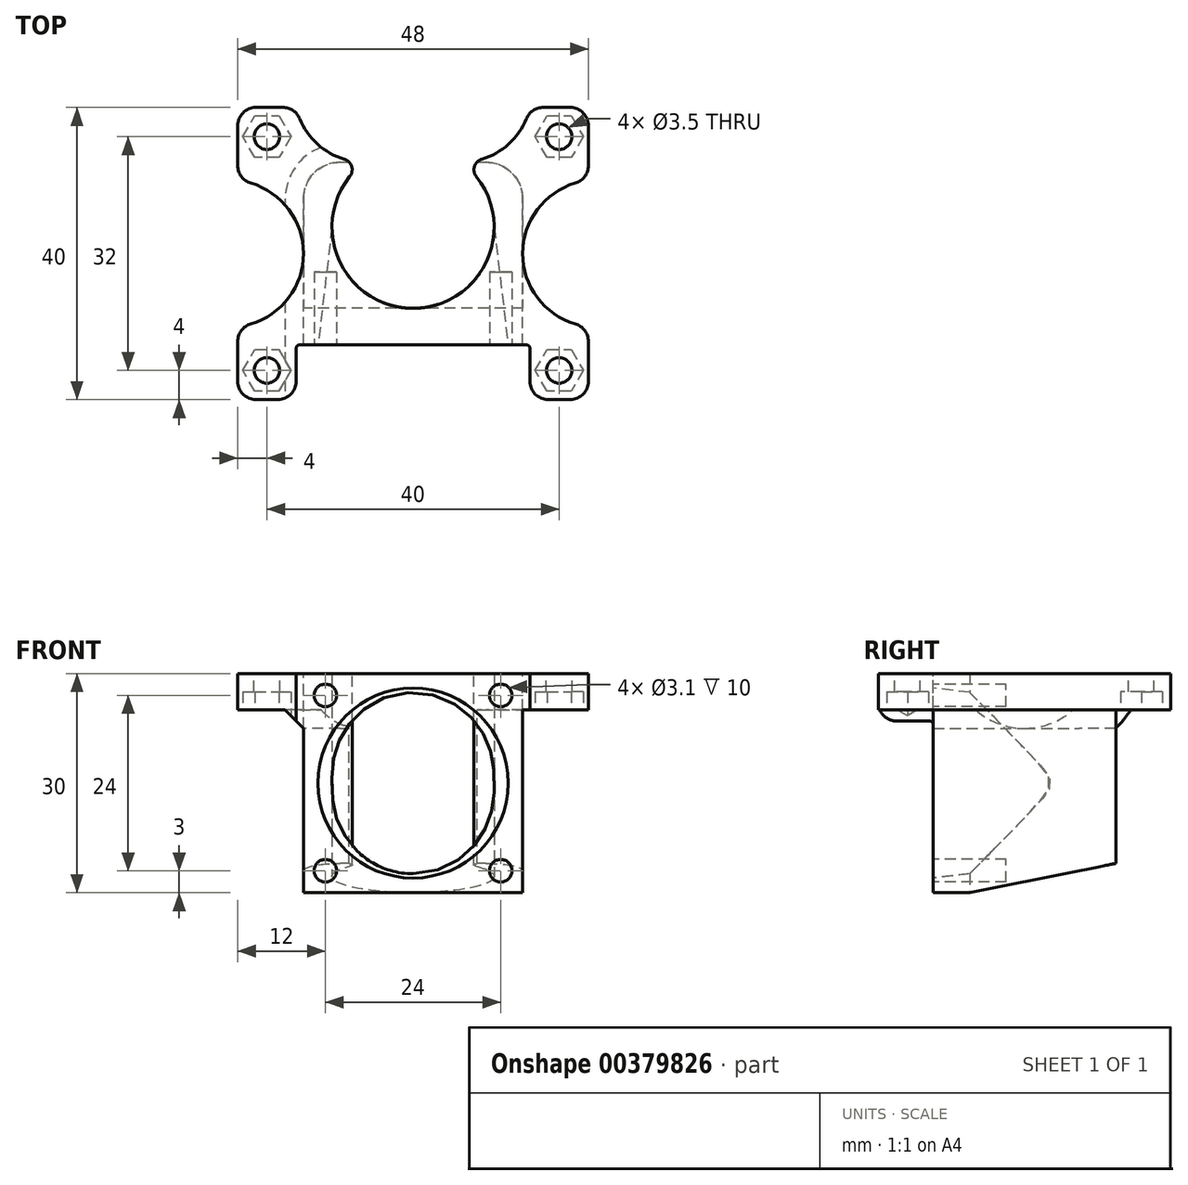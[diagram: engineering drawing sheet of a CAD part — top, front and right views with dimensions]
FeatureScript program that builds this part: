
annotation { "Feature Type Name" : "Feature", "Feature Type Description" : "" }
export const myFeature = defineFeature(function(context is Context, id is Id, definition is map)
    precondition{}
    {
        {
            var Q0;
            Q0=qCreatedBy(makeId("Top.planeOp"),FACE);
            var sketch = newSketch(context, id + "F0", { "sketchPlane" : qUnion([Q0])});
            skLineSegment(sketch, "E0.bottom", {"start": v(0, 0) * mm, "end": v(30, 0) * mm});
            skLineSegment(sketch, "E0.top", {"start": v(0, 25) * mm, "end": v(8.37, 25) * mm});
            skLineSegment(sketch, "E0.left", {"start": v(0, 0) * mm, "end": v(0, 25) * mm});
            skLineSegment(sketch, "E0.right", {"start": v(30, 0) * mm, "end": v(30, 25) * mm});
            skArc(sketch, "E1", {"start": v(8.37, 25) * mm, "mid": v(15, 5) * mm, "end": v(21.63, 25) * mm});
            skPoint(sketch, "E1.centerSnap0", {"position": v(15, 25) * mm});
            skLineSegment(sketch, "E2.trimOffspring", {"start": v(21.63, 25) * mm, "end": v(30, 25) * mm});
            skSolve(sketch);
        }
        {
            var Q0;
            Q0=qSketchRegion(id+"F0",true);
            extrude(context, id + "F1", {"entities" : qUnion([Q0]), "depth" : 30 * mm});
        }
        {
            var Q0;
            Q0=makeQuery(id+"F1.opExtrude","SWEPT_FACE",FACE,{"disambiguationData":[OSD([sQuery(id+"F0.wireOp",EDGE,"E0.left")])]});
            var sketch = newSketch(context, id + "F2", { "sketchPlane" : qUnion([Q0])});
            skLineSegment(sketch, "E3", {"start": v(-25, 4) * mm, "end": v(-5, 0) * mm});
            skLineSegment(sketch, "E4", {"start": v(-5, 0) * mm, "end": v(-25, 0) * mm});
            skLineSegment(sketch, "E5", {"start": v(-25, 0) * mm, "end": v(-25, 4) * mm});
            skSolve(sketch);
        }
        {
            var Q0;
            Q0=makeQuery(id+"F2.imprint","IMPRINT",FACE,{"disambiguationData":[TD([[makeQuery(id+"F2.imprint","IMPRINT",EDGE,{"derivedFrom":sQuery(id+"F2.wireOp",EDGE,"E3")}),-1.0]])]});
            extrude(context, id + "F3", {"entities" : qUnion([Q0]), "operationType" : NewBodyOperationType.REMOVE, "endBound" : BoundingType.THROUGH_ALL, "oppositeDirection" : true, "depth" : 25 * mm});
        }
        {
            var Q0;
            Q0=makeQuery(id+"F1.opExtrude","CAP_FACE",FACE,{"disambiguationData":[OSD([sQuery(id+"F0.wireOp",EDGE,"E0.bottom"),sQuery(id+"F0.wireOp",EDGE,"E0.top"),sQuery(id+"F0.wireOp",EDGE,"E0.left"),sQuery(id+"F0.wireOp",EDGE,"E0.right"),sQuery(id+"F0.wireOp",EDGE,"E1"),sQuery(id+"F0.wireOp",EDGE,"E2.trimOffspring")])],"isStart":false});
            cPlane(context, id + "F4", {"entities" : qUnion([Q0]), "cplaneType" : CPlaneType.OFFSET, "offset" : 15 * mm, "oppositeDirection" : true, "width" : 150 * mm, "height" : 150 * mm});
        }
        {
            var Q0;
            Q0=qCreatedBy(id+"F4.planeOp",FACE);
            var sketch = newSketch(context, id + "F5", { "sketchPlane" : qUnion([Q0])});
            skArc(sketch, "E6.0.0", {"start": v(15, 5) * mm, "mid": v(7.15, 8.25) * mm, "end": v(3.9, 16.1) * mm});
            skLineSegment(sketch, "E6.0.1", {"start": v(8.37, 25) * mm, "end": v(0, 25) * mm, "construction": true});
            skLineSegment(sketch, "E6.0.2", {"start": v(0, 25) * mm, "end": v(0, 0) * mm, "construction": true});
            skLineSegment(sketch, "E6.0.3", {"start": v(0, 0) * mm, "end": v(30, 0) * mm, "construction": true});
            skLineSegment(sketch, "E6.0.4", {"start": v(30, 0) * mm, "end": v(30, 25) * mm, "construction": true});
            skLineSegment(sketch, "E6.0.5", {"start": v(30, 25) * mm, "end": v(21.63, 25) * mm, "construction": true});
            skLineSegment(sketch, "E7", {"start": v(3.9, 16.1) * mm, "end": v(2, 0) * mm});
            skLineSegment(sketch, "E8", {"start": v(2, 0) * mm, "end": v(15, 0) * mm});
            skLineSegment(sketch, "E9", {"start": v(15, 0) * mm, "end": v(15, 5) * mm});
            skLineSegment(sketch, "E10", {"start": v(15, 16.1) * mm, "end": v(15, 5) * mm, "construction": true});
            skSolve(sketch);
        }
        {
            var Q0;
            Q0=qSketchRegion(id+"F5",true);
            var Q1;
            Q1=sQuery(id+"F5.wireOp",EDGE,"E10");
            revolve(context, id + "F6", {"operationType" : NewBodyOperationType.REMOVE, "entities" : qUnion([Q0]), "axis" : qUnion([Q1]), "revolveType" : RevolveType.FULL, "oppositeDirection" : true});
        }
        {
            var Q0;
            Q0=makeQuery(id+"F1.opExtrude","SWEPT_FACE",FACE,{"disambiguationData":[OSD([sQuery(id+"F0.wireOp",EDGE,"E0.bottom")])]});
            var sketch = newSketch(context, id + "F7", { "sketchPlane" : qUnion([Q0])});
            skCircle(sketch, "E11", {"center": v(3, 27) * mm, "radius": 1.55 * mm});
            skCircle(sketch, "E12", {"center": v(27, 27) * mm, "radius": 1.55 * mm});
            skCircle(sketch, "E13", {"center": v(27, 3) * mm, "radius": 1.55 * mm});
            skCircle(sketch, "E14", {"center": v(3, 3) * mm, "radius": 1.55 * mm});
            skSolve(sketch);
        }
        {
            var Q0;
            Q0=qSketchRegion(id+"F7",true);
            extrude(context, id + "F8", {"entities" : qUnion([Q0]), "operationType" : NewBodyOperationType.REMOVE, "oppositeDirection" : true, "depth" : 10 * mm});
        }
        {
            var Q0;
            Q0=makeQuery(id+"F1.opExtrude","CAP_FACE",FACE,{"disambiguationData":[OSD([sQuery(id+"F0.wireOp",EDGE,"E0.bottom"),sQuery(id+"F0.wireOp",EDGE,"E0.top"),sQuery(id+"F0.wireOp",EDGE,"E0.left"),sQuery(id+"F0.wireOp",EDGE,"E0.right"),sQuery(id+"F0.wireOp",EDGE,"E1"),sQuery(id+"F0.wireOp",EDGE,"E2.trimOffspring")])],"isStart":false});
            var sketch = newSketch(context, id + "F9", { "sketchPlane" : qUnion([Q0])});
            skCircle(sketch, "E15", {"center": v(35, -3.5) * mm, "radius": 1.75 * mm});
            skCircle(sketch, "E16", {"center": v(35, 28.5) * mm, "radius": 1.75 * mm});
            skLineSegment(sketch, "E17", {"start": v(31, 32.5) * mm, "end": v(39, 32.5) * mm});
            skLineSegment(sketch, "E18", {"start": v(39, 32.5) * mm, "end": v(39, 22.5) * mm});
            skPoint(sketch, "E19", {"position": v(30, 12.5) * mm});
            skLineSegment(sketch, "E20", {"start": v(30, 12.5) * mm, "end": v(39, 12.5) * mm, "construction": true});
            skLineSegment(sketch, "E21.MirrorCS", {"start": v(39, -7.5) * mm, "end": v(39, 2.5) * mm});
            skLineSegment(sketch, "E22.MirrorCS", {"start": v(31, -7.5) * mm, "end": v(39, -7.5) * mm});
            skLineSegment(sketch, "E23.MirrorCS", {"start": v(31, 0) * mm, "end": v(31, -7.5) * mm});
            skLineSegment(sketch, "E24.MirrorCS", {"start": v(30, 0) * mm, "end": v(31, 0) * mm});
            skLineSegment(sketch, "E25", {"start": v(15, 0) * mm, "end": v(15, 5) * mm, "construction": true});
            skLineSegment(sketch, "E26", {"start": v(30, 25) * mm, "end": v(21.63, 25) * mm});
            skArc(sketch, "E27", {"start": v(21.63, 25) * mm, "mid": v(27.63, 27.1) * mm, "end": v(31, 32.5) * mm});
            skArc(sketch, "E28", {"start": v(39, 22.5) * mm, "mid": v(30, 12.5) * mm, "end": v(39, 2.5) * mm});
            skLineSegment(sketch, "E29", {"start": v(30, 25) * mm, "end": v(30, 0) * mm});
            skLineSegment(sketch, "E30.MirrorCS", {"start": v(0, 0) * mm, "end": v(-1, 0) * mm});
            skLineSegment(sketch, "E31.MirrorCS", {"start": v(0, 25) * mm, "end": v(0, 0) * mm});
            skCircle(sketch, "E32.MirrorC", {"center": v(-5, -3.5) * mm, "radius": 1.75 * mm});
            skLineSegment(sketch, "E33.MirrorCS", {"start": v(-1, 32.5) * mm, "end": v(-9, 32.5) * mm});
            skLineSegment(sketch, "E34.MirrorCS", {"start": v(-9, -7.5) * mm, "end": v(-9, 2.5) * mm});
            skLineSegment(sketch, "E35.MirrorCS", {"start": v(-1, -7.5) * mm, "end": v(-9, -7.5) * mm});
            skLineSegment(sketch, "E36.MirrorCS", {"start": v(-9, 32.5) * mm, "end": v(-9, 22.5) * mm});
            skCircle(sketch, "E37.MirrorC", {"center": v(-5, 28.5) * mm, "radius": 1.75 * mm});
            skLineSegment(sketch, "E38.MirrorCS", {"start": v(0, 25) * mm, "end": v(8.37, 25) * mm});
            skPoint(sketch, "E39.MirrorP", {"position": v(0, 12.5) * mm});
            skLineSegment(sketch, "E40.MirrorCS", {"start": v(-1, 0) * mm, "end": v(-1, -7.5) * mm});
            skArc(sketch, "E41.MirrorCS", {"start": v(-9, 22.5) * mm, "mid": v(0, 12.5) * mm, "end": v(-9, 2.5) * mm});
            skArc(sketch, "E42.MirrorCS", {"start": v(8.37, 25) * mm, "mid": v(2.37, 27.1) * mm, "end": v(-1, 32.5) * mm});
            skLineSegment(sketch, "E43.MirrorCS", {"start": v(0, 12.5) * mm, "end": v(-9, 12.5) * mm, "construction": true});
            skSolve(sketch);
        }
        {
            var Q0;
            Q0=qSketchRegion(id+"F9",true);
            extrude(context, id + "F10", {"entities" : qUnion([Q0]), "operationType" : NewBodyOperationType.ADD, "oppositeDirection" : true, "depth" : 5 * mm});
        }
        {
            var Q0;
            {var subQ0=sQuery(id+"F0.wireOp",EDGE,"E0.top");var subQ1=sQuery(id+"F9.wireOp",EDGE,"fd6141a5-e393-4f37-ba07-f76781136fbe3.MirrorCS");Q0=makeQuery(id+"F10.boolean.opBoolean","SPLIT",EDGE,{"disambiguationData":[topologyDisambiguationEdgeConnected([makeQuery(id+"F10.opExtrude","SWEPT_FACE",FACE,{"disambiguationData":[OSD([subQ1]),TDD([makeQuery(id+"F9.imprint","IMPRINT",EDGE,{"disambiguationData":[TD([[makeQuery(id+"F9.imprint","INTERSECT",VERTEX,{"derivedFrom":[sQuery(id+"F9.wireOp",EDGE,"fd6141a5-e393-4f37-ba07-f76781136fbe2.MirrorCS"),subQ1]}),-1.0]])],"derivedFrom":subQ1}),makeQuery(id+"F9.imprint","IMPRINT",EDGE,{"disambiguationData":[TD([[makeQuery(id+"F9.imprint","INTERSECT",VERTEX,{"derivedFrom":[sQuery(id+"F9.wireOp",EDGE,"fd6141a5-e393-4f37-ba07-f76781136fbe1.MirrorCS"),subQ1]}),-1.0]])],"derivedFrom":subQ1})])]})])],"derivedFrom":makeQuery(id+"F1.opExtrude","SWEPT_EDGE",EDGE,{"disambiguationData":[OSD([subQ0,sQuery(id+"F0.wireOp",EDGE,"E0.left")])]})});}
            var Q1;
            {var subQ0=sQuery(id+"F0.wireOp",EDGE,"E2.trimOffspring");var subQ1=sQuery(id+"F9.wireOp",EDGE,"lfwtUtIS-q4o2-o8Hh-EETJ-Xmfctvlnuw40");Q1=makeQuery(id+"F10.boolean.opBoolean","SPLIT",EDGE,{"disambiguationData":[topologyDisambiguationEdgeConnected([makeQuery(id+"F10.opExtrude","SWEPT_FACE",FACE,{"disambiguationData":[OSD([subQ1]),TDD([makeQuery(id+"F9.imprint","IMPRINT",EDGE,{"disambiguationData":[TD([[makeQuery(id+"F9.imprint","INTERSECT",VERTEX,{"derivedFrom":[sQuery(id+"F9.wireOp",EDGE,"dHIleryw-Gs0o-nNQL-AnOp-lo5zabTGxiNF"),subQ1]}),-1.0]])],"derivedFrom":subQ1}),makeQuery(id+"F9.imprint","IMPRINT",EDGE,{"disambiguationData":[TD([[makeQuery(id+"F9.imprint","INTERSECT",VERTEX,{"derivedFrom":[subQ1,sQuery(id+"F9.wireOp",EDGE,"BK98jPus-1Hkl-NgJk-qqdw-X6xCajcux68K")]}),-1.0]])],"derivedFrom":subQ1})])]})])],"derivedFrom":makeQuery(id+"F1.opExtrude","SWEPT_EDGE",EDGE,{"disambiguationData":[OSD([sQuery(id+"F0.wireOp",EDGE,"E0.right"),subQ0])]})});}
            fillet(context, id + "F11", {"entities" : qUnion([Q0, Q1]), "radius" : 5 * mm, "tangentPropagation" : true, "allowEdgeOverflow" : false});
        }
        {
            var Q0;
            {var subQ0=sQuery(id+"F9.wireOp",EDGE,"E41.MirrorCS");var subQ1=sQuery(id+"F9.wireOp",EDGE,"E31.MirrorCS");var subQ2=sQuery(id+"F9.wireOp",EDGE,"E29");var subQ3=sQuery(id+"F9.wireOp",EDGE,"E28");Q0=makeQuery(id+"F10.boolean.opBoolean","MERGE",FACE,{"derivedFrom":[makeQuery(id+"F1.opExtrude","CAP_FACE",FACE,{"disambiguationData":[OSD([sQuery(id+"F0.wireOp",EDGE,"E0.bottom"),sQuery(id+"F0.wireOp",EDGE,"E0.top"),sQuery(id+"F0.wireOp",EDGE,"E0.left"),sQuery(id+"F0.wireOp",EDGE,"E0.right"),sQuery(id+"F0.wireOp",EDGE,"E1"),sQuery(id+"F0.wireOp",EDGE,"E2.trimOffspring")])],"isStart":false}),makeQuery(id+"F10.opExtrude","CAP_FACE",FACE,{"disambiguationData":[OSD([sQuery(id+"F9.wireOp",EDGE,"E15"),sQuery(id+"F9.wireOp",EDGE,"E21.MirrorCS"),sQuery(id+"F9.wireOp",EDGE,"E22.MirrorCS"),sQuery(id+"F9.wireOp",EDGE,"E23.MirrorCS"),sQuery(id+"F9.wireOp",EDGE,"E24.MirrorCS"),subQ3,subQ2])],"isStart":true}),makeQuery(id+"F10.opExtrude","CAP_FACE",FACE,{"disambiguationData":[OSD([sQuery(id+"F9.wireOp",EDGE,"E16"),sQuery(id+"F9.wireOp",EDGE,"E17"),sQuery(id+"F9.wireOp",EDGE,"E18"),sQuery(id+"F9.wireOp",EDGE,"E26"),sQuery(id+"F9.wireOp",EDGE,"E27"),subQ3,subQ2])],"isStart":true}),makeQuery(id+"F10.opExtrude","CAP_FACE",FACE,{"disambiguationData":[OSD([sQuery(id+"F9.wireOp",EDGE,"E30.MirrorCS"),subQ1,sQuery(id+"F9.wireOp",EDGE,"E32.MirrorC"),sQuery(id+"F9.wireOp",EDGE,"E34.MirrorCS"),sQuery(id+"F9.wireOp",EDGE,"E35.MirrorCS"),sQuery(id+"F9.wireOp",EDGE,"E40.MirrorCS"),subQ0])],"isStart":true}),makeQuery(id+"F10.opExtrude","CAP_FACE",FACE,{"disambiguationData":[OSD([subQ1,sQuery(id+"F9.wireOp",EDGE,"E33.MirrorCS"),sQuery(id+"F9.wireOp",EDGE,"E36.MirrorCS"),sQuery(id+"F9.wireOp",EDGE,"E37.MirrorC"),sQuery(id+"F9.wireOp",EDGE,"E38.MirrorCS"),subQ0,sQuery(id+"F9.wireOp",EDGE,"E42.MirrorCS")])],"isStart":true})]});}
            var sketch = newSketch(context, id + "F12", { "sketchPlane" : qUnion([Q0])});
            skArc(sketch, "E44", {"start": v(6.33, 23.04) * mm, "mid": v(6.6, 24.42) * mm, "end": v(5.6, 25.4) * mm});
            skArc(sketch, "E45.0", {"start": v(8.37, 25) * mm, "mid": v(6.97, 25.1) * mm, "end": v(5.6, 25.4) * mm});
            skArc(sketch, "E46.0", {"start": v(8.37, 25) * mm, "mid": v(7.29, 24.08) * mm, "end": v(6.33, 23.04) * mm});
            skLineSegment(sketch, "E47", {"start": v(15, 16.1) * mm, "end": v(15, 25) * mm, "construction": true});
            skArc(sketch, "E48.MirrorCS", {"start": v(23.67, 23.04) * mm, "mid": v(23.4, 24.42) * mm, "end": v(24.4, 25.4) * mm});
            skArc(sketch, "E49.MirrorCS", {"start": v(21.63, 25) * mm, "mid": v(23.03, 25.1) * mm, "end": v(24.4, 25.4) * mm});
            skPoint(sketch, "E50.orphan", {"position": v(31, 32.5) * mm});
            skArc(sketch, "E51.trimOffspring", {"start": v(23.67, 23.04) * mm, "mid": v(22.71, 24.08) * mm, "end": v(21.63, 25) * mm});
            skPoint(sketch, "E52.orphan", {"position": v(-1, 32.5) * mm});
            skSolve(sketch);
        }
        {
            var Q0;
            Q0=qSketchRegion(id+"F12",true);
            extrude(context, id + "F13", {"entities" : qUnion([Q0]), "operationType" : NewBodyOperationType.REMOVE, "endBound" : BoundingType.THROUGH_ALL, "oppositeDirection" : true, "depth" : 25 * mm});
        }
        {
            var Q0;
            Q0=makeQuery(id+"F10.opExtrude","SWEPT_EDGE",EDGE,{"disambiguationData":[OSD([sQuery(id+"F9.wireOp",EDGE,"E33.MirrorCS"),sQuery(id+"F9.wireOp",EDGE,"E36.MirrorCS")])]});
            var Q1;
            Q1=makeQuery(id+"F10.opExtrude","SWEPT_EDGE",EDGE,{"disambiguationData":[OSD([sQuery(id+"F9.wireOp",EDGE,"E36.MirrorCS"),sQuery(id+"F9.wireOp",EDGE,"E41.MirrorCS")])]});
            var Q2;
            Q2=makeQuery(id+"F10.opExtrude","SWEPT_EDGE",EDGE,{"disambiguationData":[OSD([sQuery(id+"F9.wireOp",EDGE,"E34.MirrorCS"),sQuery(id+"F9.wireOp",EDGE,"E41.MirrorCS")])]});
            var Q3;
            Q3=makeQuery(id+"F10.opExtrude","SWEPT_EDGE",EDGE,{"disambiguationData":[OSD([sQuery(id+"F9.wireOp",EDGE,"E34.MirrorCS"),sQuery(id+"F9.wireOp",EDGE,"E35.MirrorCS")])]});
            var Q4;
            Q4=makeQuery(id+"F10.opExtrude","SWEPT_EDGE",EDGE,{"disambiguationData":[OSD([sQuery(id+"F9.wireOp",EDGE,"E35.MirrorCS"),sQuery(id+"F9.wireOp",EDGE,"E40.MirrorCS")])]});
            var Q5;
            Q5=makeQuery(id+"F10.opExtrude","SWEPT_EDGE",EDGE,{"disambiguationData":[OSD([sQuery(id+"F9.wireOp",EDGE,"E18"),sQuery(id+"F9.wireOp",EDGE,"E28")])]});
            var Q6;
            Q6=makeQuery(id+"F10.opExtrude","SWEPT_EDGE",EDGE,{"disambiguationData":[OSD([sQuery(id+"F9.wireOp",EDGE,"E21.MirrorCS"),sQuery(id+"F9.wireOp",EDGE,"E22.MirrorCS")])]});
            var Q7;
            Q7=makeQuery(id+"F10.opExtrude","SWEPT_EDGE",EDGE,{"disambiguationData":[OSD([sQuery(id+"F9.wireOp",EDGE,"E22.MirrorCS"),sQuery(id+"F9.wireOp",EDGE,"E23.MirrorCS")])]});
            var Q8;
            Q8=makeQuery(id+"F10.opExtrude","SWEPT_EDGE",EDGE,{"disambiguationData":[OSD([sQuery(id+"F9.wireOp",EDGE,"E21.MirrorCS"),sQuery(id+"F9.wireOp",EDGE,"E28")])]});
            var Q9;
            Q9=makeQuery(id+"F10.opExtrude","SWEPT_EDGE",EDGE,{"disambiguationData":[OSD([sQuery(id+"F9.wireOp",EDGE,"E17"),sQuery(id+"F9.wireOp",EDGE,"E18")])]});
            var Q10;
            Q10=makeQuery(id+"F10.opExtrude","SWEPT_EDGE",EDGE,{"disambiguationData":[OSD([sQuery(id+"F9.wireOp",EDGE,"E17"),sQuery(id+"F9.wireOp",EDGE,"E27")])]});
            var Q11;
            Q11=makeQuery(id+"F10.opExtrude","SWEPT_EDGE",EDGE,{"disambiguationData":[OSD([sQuery(id+"F9.wireOp",EDGE,"E33.MirrorCS"),sQuery(id+"F9.wireOp",EDGE,"E42.MirrorCS")])]});
            fillet(context, id + "F14", {"entities" : qUnion([Q0, Q1, Q2, Q3, Q4, Q5, Q6, Q7, Q8, Q9, Q10, Q11]), "radius" : 2.5 * mm, "tangentPropagation" : true, "allowEdgeOverflow" : false});
        }
        {
            var Q0;
            {var subQ0=sQuery(id+"F9.wireOp",EDGE,"E29");Q0=makeQuery(id+"F10.opExtrude","CAP_EDGE",EDGE,{"disambiguationData":[OSD([subQ0]),TDD([makeQuery(id+"F9.imprint","IMPRINT",EDGE,{"disambiguationData":[TD([[makeQuery(id+"F9.imprint","INTERSECT",VERTEX,{"derivedFrom":[sQuery(id+"F9.wireOp",EDGE,"E28"),subQ0]}),1.0]])],"derivedFrom":subQ0})])],"isStart":false});}
            var Q1;
            Q1=makeQuery(id+"F11.opFillet","BLEND_EDGE",EDGE,{"blendedFrom":[makeQuery(id+"F1.opExtrude","SWEPT_EDGE",EDGE,{"disambiguationData":[OSD([sQuery(id+"F0.wireOp",EDGE,"E0.top"),sQuery(id+"F0.wireOp",EDGE,"E0.left")])]}),makeQuery(id+"F10.opExtrude","CAP_FACE",FACE,{"disambiguationData":[OSD([sQuery(id+"F9.wireOp",EDGE,"E31.MirrorCS"),sQuery(id+"F9.wireOp",EDGE,"E33.MirrorCS"),sQuery(id+"F9.wireOp",EDGE,"E36.MirrorCS"),sQuery(id+"F9.wireOp",EDGE,"E37.MirrorC"),sQuery(id+"F9.wireOp",EDGE,"E38.MirrorCS"),sQuery(id+"F9.wireOp",EDGE,"E41.MirrorCS"),sQuery(id+"F9.wireOp",EDGE,"E42.MirrorCS")])],"isStart":false})],"blendedInto":[makeQuery(id+"F10.opExtrude","CAP_FACE",FACE,{"disambiguationData":[OSD([sQuery(id+"F9.wireOp",EDGE,"E31.MirrorCS"),sQuery(id+"F9.wireOp",EDGE,"E33.MirrorCS"),sQuery(id+"F9.wireOp",EDGE,"E36.MirrorCS"),sQuery(id+"F9.wireOp",EDGE,"E37.MirrorC"),sQuery(id+"F9.wireOp",EDGE,"E38.MirrorCS"),sQuery(id+"F9.wireOp",EDGE,"E41.MirrorCS"),sQuery(id+"F9.wireOp",EDGE,"E42.MirrorCS")])],"isStart":false})]});
            chamfer(context, id + "F15", {"entities" : qUnion([Q0, Q1]), "width" : 2.5 * mm, "tangentPropagation" : true});
        }
        {
            var Q0;
            Q0=makeQuery(id+"F10.opExtrude","CAP_FACE",FACE,{"disambiguationData":[OSD([sQuery(id+"F9.wireOp",EDGE,"E30.MirrorCS"),sQuery(id+"F9.wireOp",EDGE,"E31.MirrorCS"),sQuery(id+"F9.wireOp",EDGE,"E32.MirrorC"),sQuery(id+"F9.wireOp",EDGE,"E34.MirrorCS"),sQuery(id+"F9.wireOp",EDGE,"E35.MirrorCS"),sQuery(id+"F9.wireOp",EDGE,"E40.MirrorCS"),sQuery(id+"F9.wireOp",EDGE,"E41.MirrorCS")])],"isStart":false});
            var sketch = newSketch(context, id + "F16", { "sketchPlane" : qUnion([Q0])});
            skCircle(sketch, "E53.cCircle", {"center": v(-5, 3.5) * mm, "radius": 2.85 * mm, "construction": true});
            skLineSegment(sketch, "E53.0", {"start": v(-6.65, 6.35) * mm, "end": v(-3.35, 6.35) * mm});
            skLineSegment(sketch, "E53.1", {"start": v(-3.35, 6.35) * mm, "end": v(-1.7, 3.5) * mm});
            skLineSegment(sketch, "E53.2", {"start": v(-1.7, 3.5) * mm, "end": v(-3.35, 0.65) * mm});
            skLineSegment(sketch, "E53.3", {"start": v(-3.35, 0.65) * mm, "end": v(-6.65, 0.65) * mm});
            skLineSegment(sketch, "E53.4", {"start": v(-6.65, 0.65) * mm, "end": v(-8.3, 3.5) * mm});
            skLineSegment(sketch, "E53.5", {"start": v(-8.3, 3.5) * mm, "end": v(-6.65, 6.35) * mm});
            skPoint(sketch, "E53.0.midPoint", {"position": v(-5, 6.35) * mm});
            skCircle(sketch, "E54.0", {"center": v(-5, -28.5) * mm, "radius": 1.75 * mm, "construction": true});
            skCircle(sketch, "E55.0", {"center": v(35, -28.5) * mm, "radius": 1.75 * mm, "construction": true});
            skCircle(sketch, "E56.0", {"center": v(35, 3.5) * mm, "radius": 1.75 * mm, "construction": true});
            skCircle(sketch, "E57.cCircle", {"center": v(35, 3.5) * mm, "radius": 2.85 * mm, "construction": true});
            skLineSegment(sketch, "E57.0", {"start": v(36.65, 0.65) * mm, "end": v(33.35, 0.65) * mm});
            skLineSegment(sketch, "E57.1", {"start": v(33.35, 0.65) * mm, "end": v(31.7, 3.5) * mm});
            skLineSegment(sketch, "E57.2", {"start": v(31.7, 3.5) * mm, "end": v(33.35, 6.35) * mm});
            skLineSegment(sketch, "E57.3", {"start": v(33.35, 6.35) * mm, "end": v(36.65, 6.35) * mm});
            skLineSegment(sketch, "E57.4", {"start": v(36.65, 6.35) * mm, "end": v(38.3, 3.5) * mm});
            skLineSegment(sketch, "E57.5", {"start": v(38.3, 3.5) * mm, "end": v(36.65, 0.65) * mm});
            skPoint(sketch, "E57.0.midPoint", {"position": v(35, 0.65) * mm});
            skCircle(sketch, "E58.cCircle", {"center": v(35, -28.5) * mm, "radius": 2.85 * mm, "construction": true});
            skLineSegment(sketch, "E58.0", {"start": v(33.35, -25.65) * mm, "end": v(36.65, -25.65) * mm});
            skLineSegment(sketch, "E58.1", {"start": v(36.65, -25.65) * mm, "end": v(38.3, -28.5) * mm});
            skLineSegment(sketch, "E58.2", {"start": v(38.3, -28.5) * mm, "end": v(36.65, -31.35) * mm});
            skLineSegment(sketch, "E58.3", {"start": v(36.65, -31.35) * mm, "end": v(33.35, -31.35) * mm});
            skLineSegment(sketch, "E58.4", {"start": v(33.35, -31.35) * mm, "end": v(31.7, -28.5) * mm});
            skLineSegment(sketch, "E58.5", {"start": v(31.7, -28.5) * mm, "end": v(33.35, -25.65) * mm});
            skPoint(sketch, "E58.0.midPoint", {"position": v(35, -25.65) * mm});
            skCircle(sketch, "E59.cCircle", {"center": v(-5, -28.5) * mm, "radius": 2.85 * mm, "construction": true});
            skLineSegment(sketch, "E59.0", {"start": v(-6.65, -25.65) * mm, "end": v(-3.35, -25.65) * mm});
            skLineSegment(sketch, "E59.1", {"start": v(-3.35, -25.65) * mm, "end": v(-1.7, -28.5) * mm});
            skLineSegment(sketch, "E59.2", {"start": v(-1.7, -28.5) * mm, "end": v(-3.35, -31.35) * mm});
            skLineSegment(sketch, "E59.3", {"start": v(-3.35, -31.35) * mm, "end": v(-6.65, -31.35) * mm});
            skLineSegment(sketch, "E59.4", {"start": v(-6.65, -31.35) * mm, "end": v(-8.3, -28.5) * mm});
            skLineSegment(sketch, "E59.5", {"start": v(-8.3, -28.5) * mm, "end": v(-6.65, -25.65) * mm});
            skPoint(sketch, "E59.0.midPoint", {"position": v(-5, -25.65) * mm});
            skSolve(sketch);
        }
        {
            var Q0;
            Q0=qSketchRegion(id+"F16",true);
            extrude(context, id + "F17", {"entities" : qUnion([Q0]), "operationType" : NewBodyOperationType.REMOVE, "oppositeDirection" : true, "depth" : 2.5 * mm, "hasSecondDirection" : true, "secondDirectionBound" : SecondDirectionBoundingType.THROUGH_ALL, "secondDirectionOppositeDirection" : false, "secondDirectionDepth" : 25 * mm});
        }
        {
            var Q0;
            Q0=makeQuery(id+"F10.opExtrude","SWEPT_EDGE",EDGE,{"disambiguationData":[OSD([sQuery(id+"F9.wireOp",EDGE,"E23.MirrorCS"),sQuery(id+"F9.wireOp",EDGE,"E24.MirrorCS")])]});
            var Q1;
            Q1=makeQuery(id+"F10.opExtrude","SWEPT_EDGE",EDGE,{"disambiguationData":[OSD([sQuery(id+"F9.wireOp",EDGE,"E30.MirrorCS"),sQuery(id+"F9.wireOp",EDGE,"E40.MirrorCS")])]});
            fillet(context, id + "F18", {"entities" : qUnion([Q0, Q1]), "radius" : .5 * mm, "tangentPropagation" : true, "allowEdgeOverflow" : false});
        }
    });
